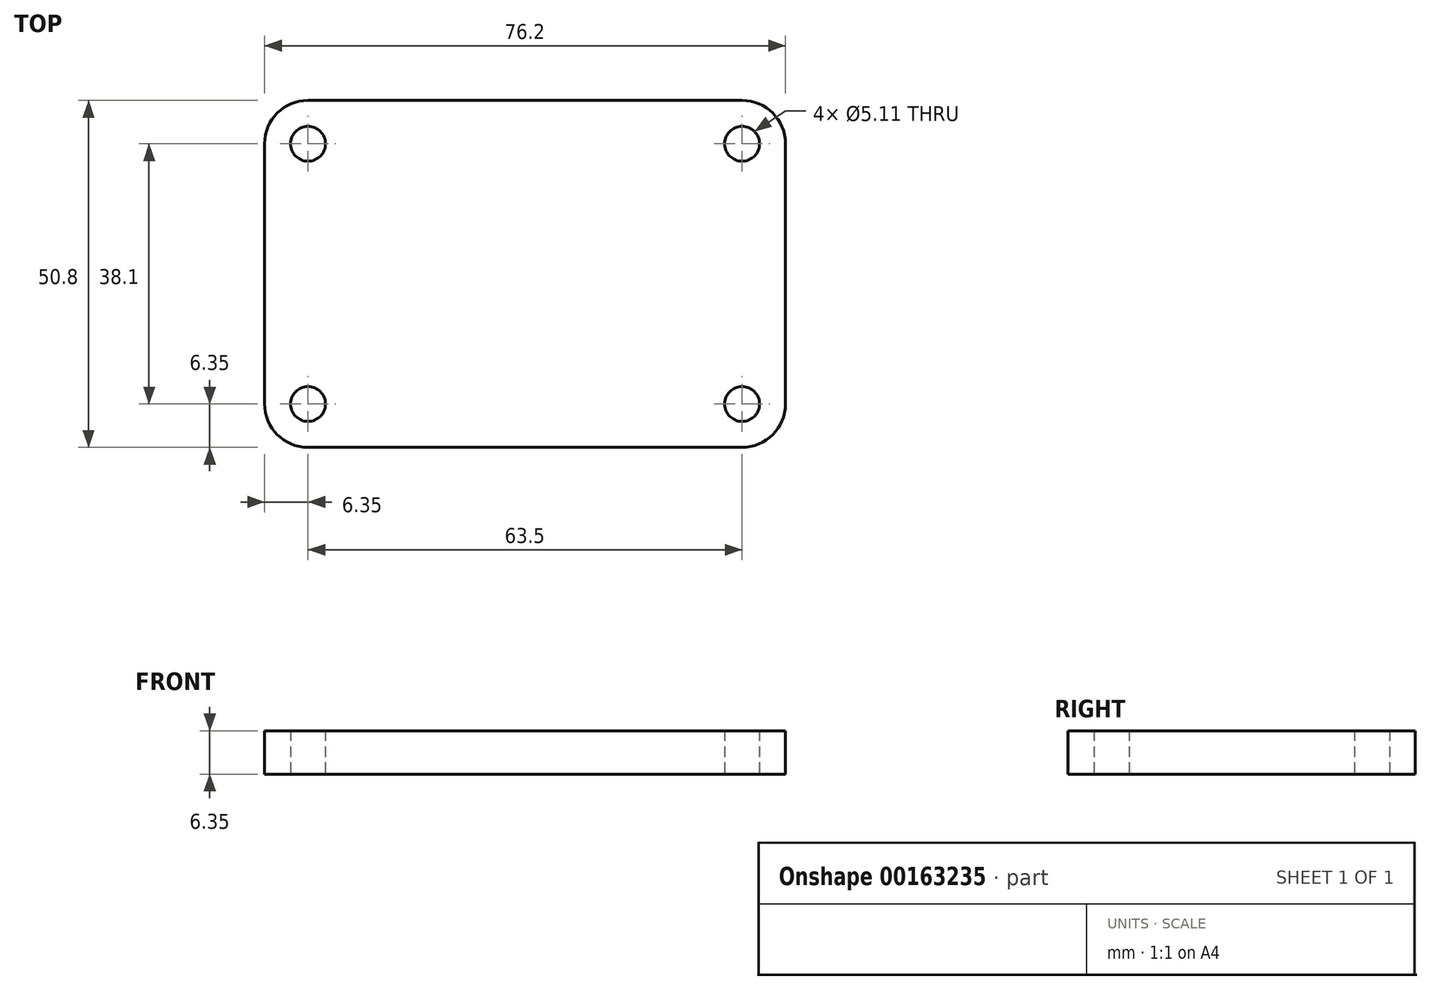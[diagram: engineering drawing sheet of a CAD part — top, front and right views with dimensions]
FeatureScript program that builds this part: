
annotation { "Feature Type Name" : "Feature", "Feature Type Description" : "" }
export const myFeature = defineFeature(function(context is Context, id is Id, definition is map)
    precondition{}
    {
        {
            var Q0;
            Q0=qCreatedBy(makeId("Top.planeOp"),FACE);
            var sketch = newSketch(context, id + "F0", { "sketchPlane" : qUnion([Q0])});
            skLineSegment(sketch, "E0.bottom", {"start": v(-38.1, 25.4) * mm, "end": v(38.1, 25.4) * mm});
            skLineSegment(sketch, "E0.top", {"start": v(-38.1, -25.4) * mm, "end": v(38.1, -25.4) * mm});
            skLineSegment(sketch, "E0.left", {"start": v(-38.1, 25.4) * mm, "end": v(-38.1, -25.4) * mm});
            skLineSegment(sketch, "E0.right", {"start": v(38.1, 25.4) * mm, "end": v(38.1, -25.4) * mm});
            skCircle(sketch, "E1", {"center": v(31.75, 19.05) * mm, "radius": 2.55 * mm});
            skCircle(sketch, "E2", {"center": v(31.75, -19.05) * mm, "radius": 2.55 * mm});
            skCircle(sketch, "E3", {"center": v(-31.75, -19.05) * mm, "radius": 2.55 * mm});
            skCircle(sketch, "E4", {"center": v(-31.75, 19.05) * mm, "radius": 2.55 * mm});
            skSolve(sketch);
        }
        {
            var Q0;
            Q0 = qSketchRegion(id + "F0", true);
            extrude(context, id + "F2", {"entities" : qUnion([Q0]), "depth" : 6.35 * mm});
        }
        {
            var Q0;
            Q0=makeQuery(id+"F2.opExtrude","SWEPT_EDGE",EDGE,{"disambiguationData":[OSD([sQuery(id+"F0.wireOp",EDGE,"E0.bottom"),sQuery(id+"F0.wireOp",EDGE,"E0.left")])]});
            var Q1;
            Q1=makeQuery(id+"F2.opExtrude","SWEPT_EDGE",EDGE,{"disambiguationData":[OSD([sQuery(id+"F0.wireOp",EDGE,"E0.top"),sQuery(id+"F0.wireOp",EDGE,"E0.left")])]});
            var Q2;
            Q2=makeQuery(id+"F2.opExtrude","SWEPT_EDGE",EDGE,{"disambiguationData":[OSD([sQuery(id+"F0.wireOp",EDGE,"E0.bottom"),sQuery(id+"F0.wireOp",EDGE,"E0.right")])]});
            var Q3;
            Q3=makeQuery(id+"F2.opExtrude","SWEPT_EDGE",EDGE,{"disambiguationData":[OSD([sQuery(id+"F0.wireOp",EDGE,"E0.top"),sQuery(id+"F0.wireOp",EDGE,"E0.right")])]});
            fillet(context, id + "F1", {"entities" : qUnion([Q0, Q1, Q2, Q3]), "radius" : 6.35 * mm, "tangentPropagation" : true, "allowEdgeOverflow" : false});
        }
    });
